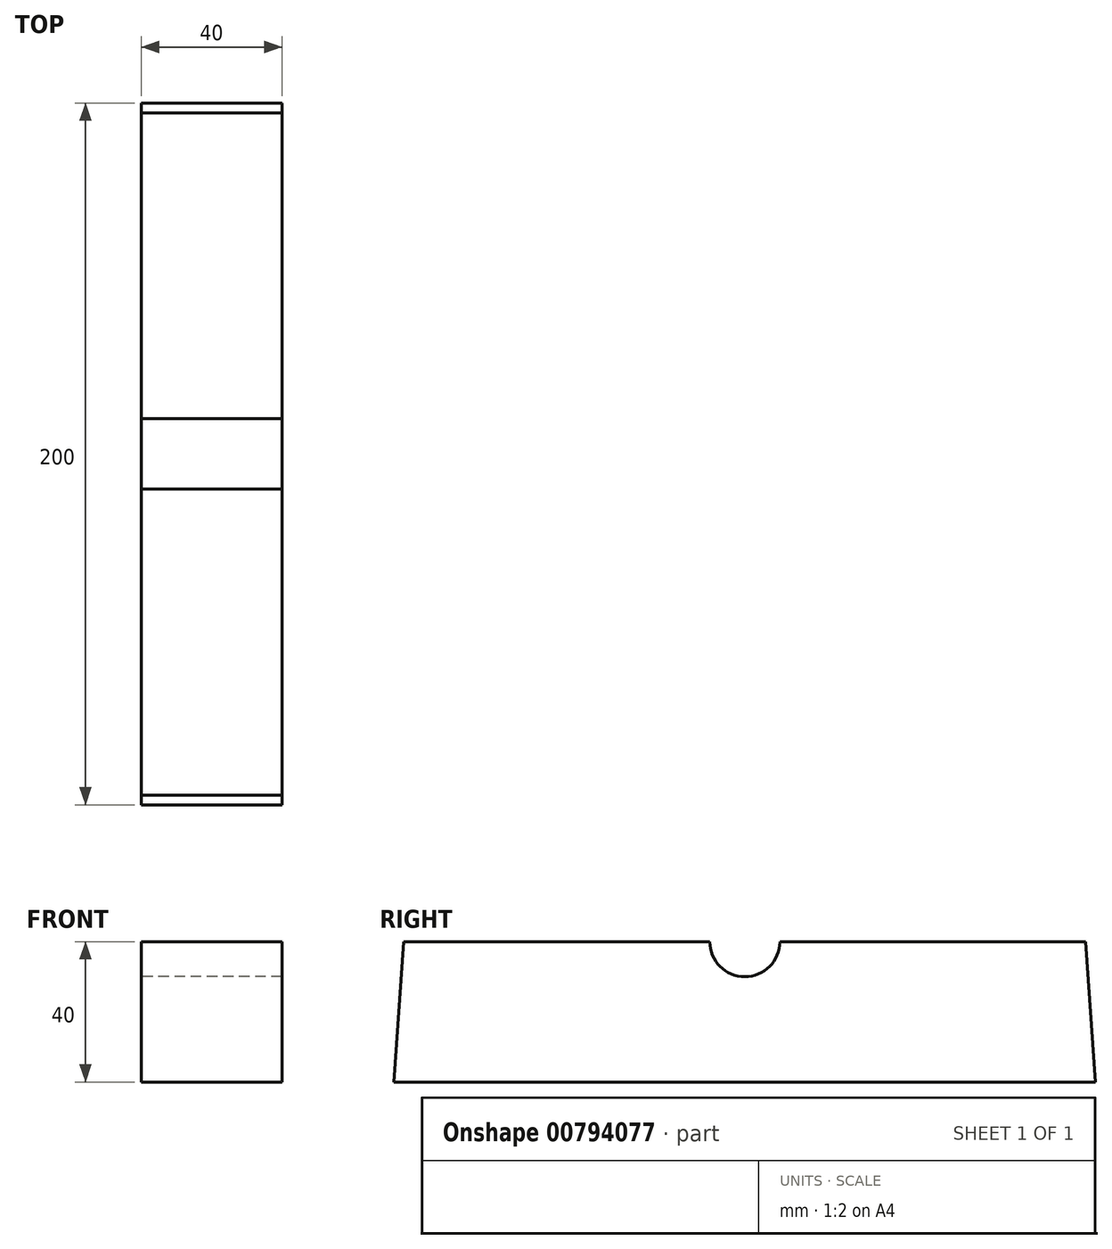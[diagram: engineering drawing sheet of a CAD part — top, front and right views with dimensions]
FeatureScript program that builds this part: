
annotation { "Feature Type Name" : "Feature", "Feature Type Description" : "" }
export const myFeature = defineFeature(function(context is Context, id is Id, definition is map)
    precondition{}
    {
        {
            var Q0;
            Q0=qCreatedBy(makeId("Right.planeOp"),FACE);
            var sketch = newSketch(context, id + "F0", { "sketchPlane" : qUnion([Q0])});
            skLineSegment(sketch, "E0.bottom", {"start": v(0, 0) * mm, "end": v(-200, 0) * mm});
            skLineSegment(sketch, "E0.top", {"start": v(-2.8, 40) * mm, "end": v(-90, 40) * mm});
            skLineSegment(sketch, "E1", {"start": v(0, 0) * mm, "end": v(-3.37, 48.15) * mm});
            skLineSegment(sketch, "E2", {"start": v(-200, 0) * mm, "end": v(-196.58, 48.94) * mm});
            skArc(sketch, "E3", {"start": v(-110, 40) * mm, "mid": v(-100, 30) * mm, "end": v(-90, 40) * mm});
            skLineSegment(sketch, "E4.trimOffspring", {"start": v(-110, 40) * mm, "end": v(-197.2, 40) * mm});
            skSolve(sketch);
        }
        {
            var Q0;
            Q0 = qSketchRegion(id + "F0", true);
            extrude(context, id + "F1", {"entities" : qUnion([Q0]), "depth" : 40 * mm, "offsetDistance" : 25 * mm});
        }
    });
